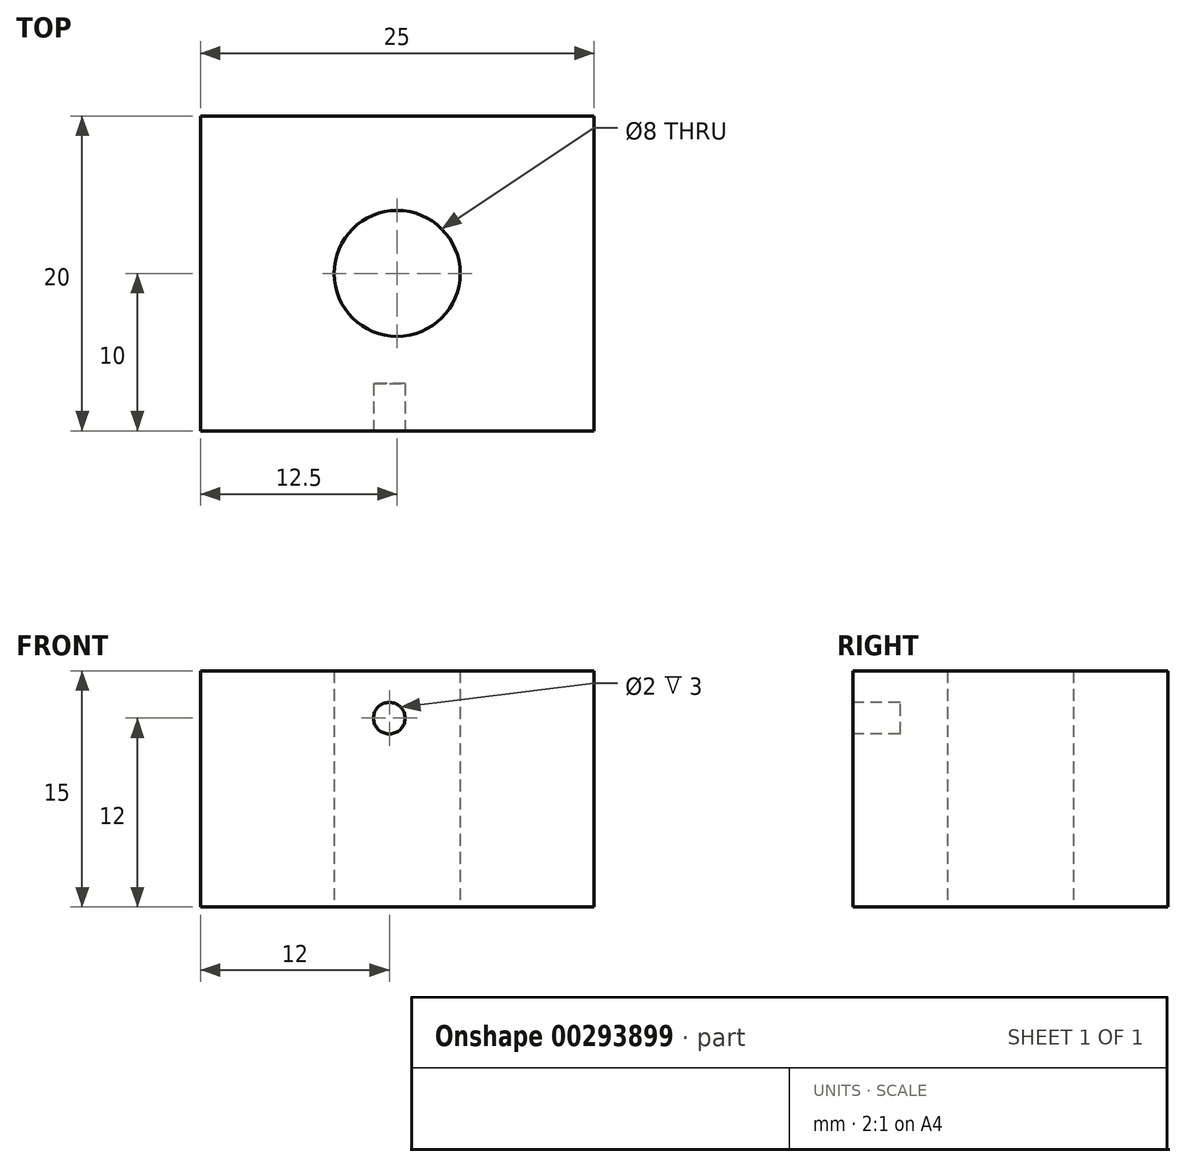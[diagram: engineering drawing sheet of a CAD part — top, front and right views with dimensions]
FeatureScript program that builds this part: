
annotation { "Feature Type Name" : "Feature", "Feature Type Description" : "" }
export const myFeature = defineFeature(function(context is Context, id is Id, definition is map)
    precondition{}
    {
        {
            var Q0;
            Q0=qCreatedBy(makeId("Top.planeOp"),FACE);
            var sketch = newSketch(context, id + "F0", { "sketchPlane" : qUnion([Q0])});
            skLineSegment(sketch, "E0.bottom", {"start": v(0, 0) * mm, "end": v(25, 0) * mm});
            skLineSegment(sketch, "E0.top", {"start": v(0, 20) * mm, "end": v(25, 20) * mm});
            skLineSegment(sketch, "E0.left", {"start": v(0, 0) * mm, "end": v(0, 20) * mm});
            skLineSegment(sketch, "E0.right", {"start": v(25, 0) * mm, "end": v(25, 20) * mm});
            skCircle(sketch, "E1", {"center": v(12.5, 10) * mm, "radius": 4 * mm});
            skLineSegment(sketch, "E2", {"start": v(12.5, 10) * mm, "end": v(12.5, 20) * mm, "construction": true});
            skLineSegment(sketch, "E3", {"start": v(12.5, 10) * mm, "end": v(0, 10) * mm, "construction": true});
            skSolve(sketch);
        }
        {
            var Q0;
            Q0=makeQuery(id+"F0.imprint","IMPRINT",FACE,{"disambiguationData":[TD([[makeQuery(id+"F0.imprint","IMPRINT",EDGE,{"derivedFrom":sQuery(id+"F0.wireOp",EDGE,"E0.bottom")}),1.0]])]});
            extrude(context, id + "F1", {"entities" : qUnion([Q0]), "depth" : 15 * mm});
        }
        {
            var Q0;
            Q0=makeQuery(id+"F1.opExtrude","SWEPT_FACE",FACE,{"disambiguationData":[OSD([sQuery(id+"F0.wireOp",EDGE,"E0.bottom")])]});
            var sketch = newSketch(context, id + "F2", { "sketchPlane" : qUnion([Q0])});
            skCircle(sketch, "E4", {"center": v(12, 12) * mm, "radius": 1 * mm});
            skSolve(sketch);
        }
        {
            var Q0;
            Q0=makeQuery(id+"F2.imprint","IMPRINT",FACE,{"disambiguationData":[TD([[makeQuery(id+"F2.imprint","IMPRINT",EDGE,{"derivedFrom":sQuery(id+"F2.wireOp",EDGE,"E4")}),1.0]])]});
            extrude(context, id + "F3", {"entities" : qUnion([Q0]), "operationType" : NewBodyOperationType.REMOVE, "oppositeDirection" : true, "depth" : 3 * mm});
        }
    });
